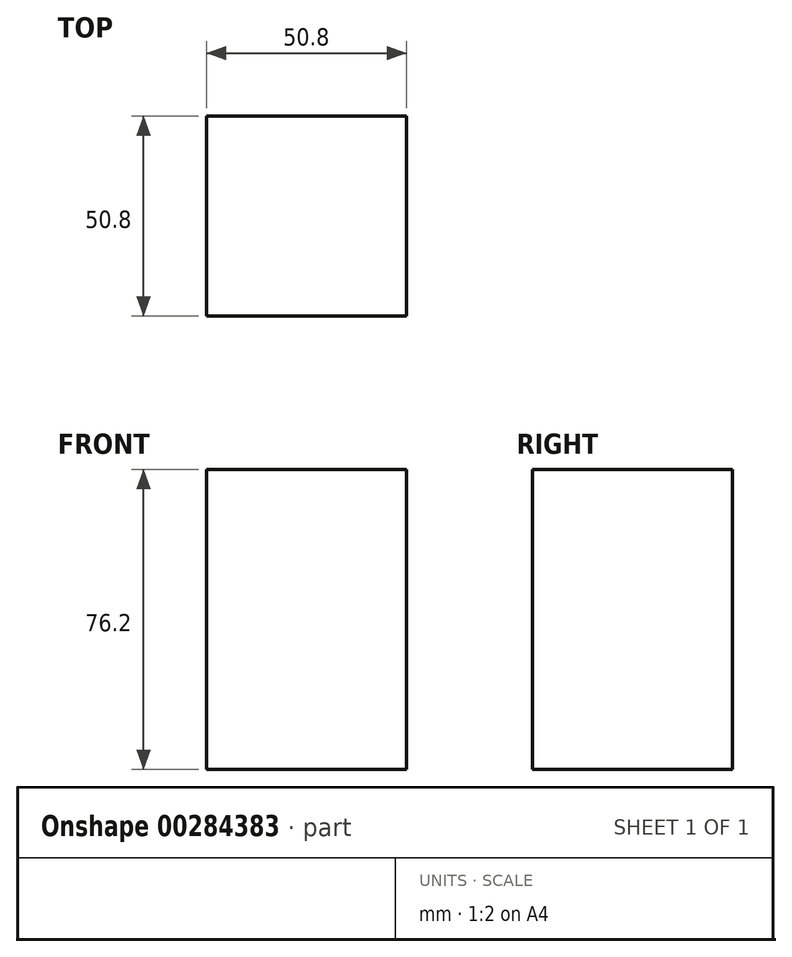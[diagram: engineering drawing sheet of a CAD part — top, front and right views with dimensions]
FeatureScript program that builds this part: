
annotation { "Feature Type Name" : "Feature", "Feature Type Description" : "" }
export const myFeature = defineFeature(function(context is Context, id is Id, definition is map)
    precondition{}
    {
        {
            var Q0;
            Q0=qCreatedBy(makeId("Front.planeOp"),FACE);
            var sketch = newSketch(context, id + "F1", { "sketchPlane" : qUnion([Q0])});
            skLineSegment(sketch, "E0.bottom", {"start": v(0, 0) * mm, "end": v(50.8, 0) * mm});
            skLineSegment(sketch, "E0.top", {"start": v(0, 76.2) * mm, "end": v(50.8, 76.2) * mm});
            skLineSegment(sketch, "E0.left", {"start": v(0, 0) * mm, "end": v(0, 76.2) * mm});
            skLineSegment(sketch, "E0.right", {"start": v(50.8, 0) * mm, "end": v(50.8, 76.2) * mm});
            skSolve(sketch);
        }
        {
            var Q0;
            Q0 = qSketchRegion(id + "F1", true);
            extrude(context, id + "F0", {"entities" : qUnion([Q0]), "depth" : 50.8 * mm});
        }
    });
